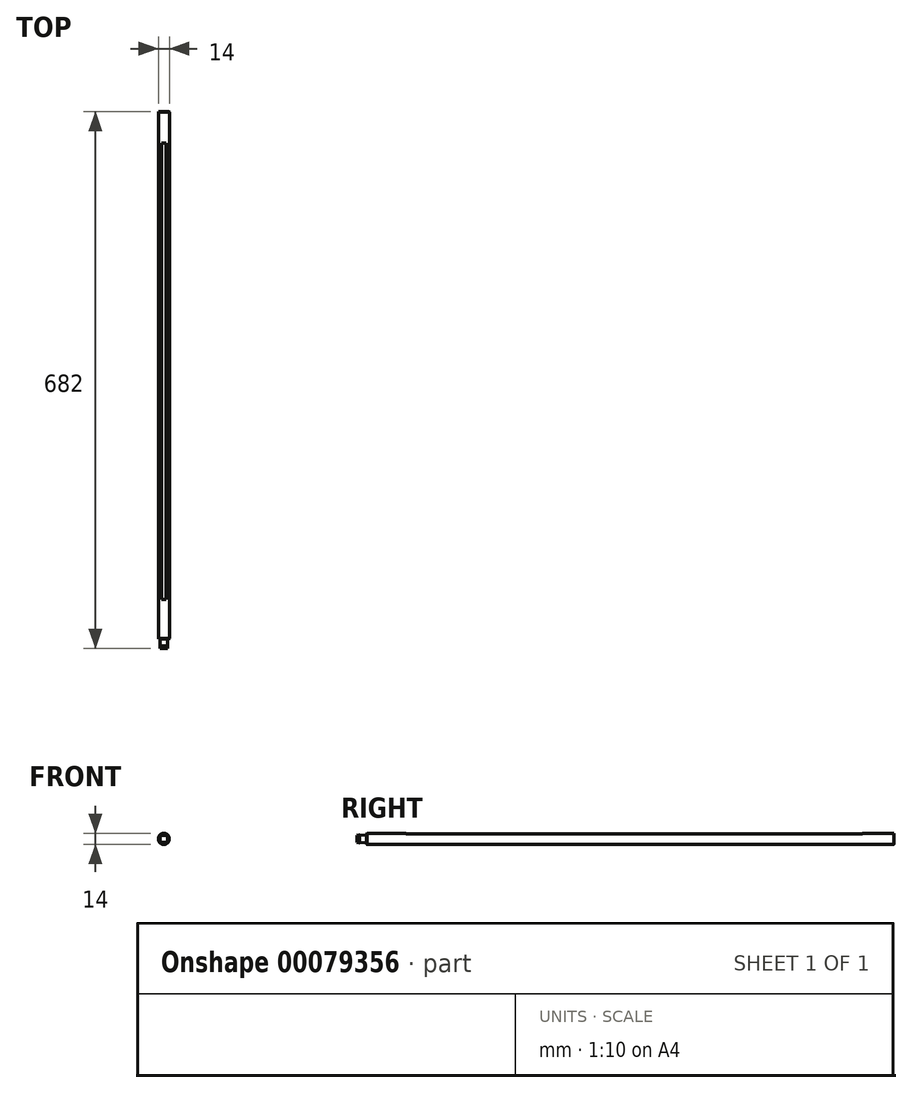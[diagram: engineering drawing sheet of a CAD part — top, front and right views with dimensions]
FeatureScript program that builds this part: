
annotation { "Feature Type Name" : "Feature", "Feature Type Description" : "" }
export const myFeature = defineFeature(function(context is Context, id is Id, definition is map)
    precondition{}
    {
        {
            var Q0;
            Q0=qCreatedBy(makeId("Front.planeOp"),FACE);
            var sketch = newSketch(context, id + "F0", { "sketchPlane" : qUnion([Q0])});
            skCircle(sketch, "E0", {"center": v(0, 0) * mm, "radius": 7 * mm});
            skSolve(sketch);
        }
        {
            var Q0;
            Q0=makeQuery(id+"F0.imprint","IMPRINT",FACE,{"disambiguationData":[TD([[makeQuery(id+"F0.imprint","IMPRINT",EDGE,{"derivedFrom":sQuery(id+"F0.wireOp",EDGE,"E0")}),1.0]])]});
            extrude(context, id + "F1", {"entities" : qUnion([Q0]), "oppositeDirection" : true, "depth" : 670 * mm});
        }
        {
            var Q0;
            Q0=qCreatedBy(makeId("Front.planeOp"),FACE);
            var sketch = newSketch(context, id + "F2", { "sketchPlane" : qUnion([Q0])});
            skLineSegment(sketch, "E1.top", {"start": v(-5, 5) * mm, "end": v(5, 5) * mm});
            skLineSegment(sketch, "E1.left", {"start": v(-5, 4.92) * mm, "end": v(-5, 5) * mm});
            skLineSegment(sketch, "E1.right", {"start": v(5, 4.92) * mm, "end": v(5, 5) * mm});
            skLineSegment(sketch, "E2", {"start": v(-5, 5) * mm, "end": v(-5, -5) * mm});
            skLineSegment(sketch, "E3", {"start": v(-5, -5) * mm, "end": v(5, -5) * mm});
            skLineSegment(sketch, "E4", {"start": v(5, 5) * mm, "end": v(5, -5) * mm});
            skSolve(sketch);
        }
        {
            var Q0;
            {var subQ0=sQuery(id+"F2.wireOp",EDGE,"E1.top");Q0=makeQuery(id+"F2.imprint","IMPRINT",FACE,{"disambiguationData":[TD([[makeQuery(id+"F2.imprint","IMPRINT",EDGE,{"derivedFrom":subQ0}),-1.0]])]});}
            extrude(context, id + "F3", {"entities" : qUnion([Q0]), "depth" : 12 * mm});
        }
        {
            var Q0;
            Q0=makeQuery(id+"F3.opExtrude","SWEPT_FACE",FACE,{"disambiguationData":[OSD([sQuery(id+"F2.wireOp",EDGE,"E4")])]});
            var sketch = newSketch(context, id + "F4", { "sketchPlane" : qUnion([Q0])});
            skLineSegment(sketch, "E5", {"start": v(-12, -4.5) * mm, "end": v(-9, -5) * mm});
            skLineSegment(sketch, "E6", {"start": v(-9, 5) * mm, "end": v(-12, 4.5) * mm});
            skSolve(sketch);
        }
        {
            var Q0;
            {var subQ0=sQuery(id+"F4.wireOp",EDGE,"E5");Q0=makeQuery(id+"F4.imprint","IMPRINT",FACE,{"disambiguationData":[TD([[makeQuery(id+"F4.imprint","IMPRINT",EDGE,{"derivedFrom":subQ0}),-1.0]])]});}
            extrude(context, id + "F5", {"entities" : qUnion([Q0]), "operationType" : NewBodyOperationType.REMOVE, "oppositeDirection" : true, "depth" : 25 * mm});
        }
        {
            var Q0;
            Q0=makeQuery(id+"F3.opExtrude","SWEPT_FACE",FACE,{"disambiguationData":[OSD([sQuery(id+"F2.wireOp",EDGE,"E1.top")])]});
            var sketch = newSketch(context, id + "F6", { "sketchPlane" : qUnion([Q0])});
            skLineSegment(sketch, "E7", {"start": v(4.5, -12) * mm, "end": v(5, -9) * mm});
            skLineSegment(sketch, "E8", {"start": v(-4.5, -12) * mm, "end": v(-5, -9) * mm});
            skSolve(sketch);
        }
        {
            var Q0;
            {var subQ0=sQuery(id+"F6.wireOp",EDGE,"E7");Q0=makeQuery(id+"F6.imprint","IMPRINT",FACE,{"disambiguationData":[TD([[makeQuery(id+"F6.imprint","IMPRINT",EDGE,{"derivedFrom":subQ0}),-1.0]])]});}
            extrude(context, id + "F7", {"entities" : qUnion([Q0]), "operationType" : NewBodyOperationType.REMOVE, "oppositeDirection" : true, "depth" : 25 * mm});
        }
        {
            var Q0;
            {var subQ0=sQuery(id+"F6.wireOp",EDGE,"E8");Q0=makeQuery(id+"F6.imprint","IMPRINT",FACE,{"disambiguationData":[TD([[makeQuery(id+"F6.imprint","IMPRINT",EDGE,{"derivedFrom":subQ0}),1.0]])]});}
            extrude(context, id + "F8", {"entities" : qUnion([Q0]), "operationType" : NewBodyOperationType.REMOVE, "oppositeDirection" : true, "depth" : 25 * mm});
        }
        {
            var Q0;
            {var subQ0=sQuery(id+"F4.wireOp",EDGE,"E6");Q0=makeQuery(id+"F4.imprint","IMPRINT",FACE,{"disambiguationData":[TD([[makeQuery(id+"F4.imprint","IMPRINT",EDGE,{"derivedFrom":subQ0}),-1.0]])]});}
            extrude(context, id + "F9", {"entities" : qUnion([Q0]), "operationType" : NewBodyOperationType.REMOVE, "oppositeDirection" : true, "depth" : 25 * mm});
        }
        {
            var Q0;
            Q0=makeQuery(id+"F3.opExtrude","SWEPT_FACE",FACE,{"disambiguationData":[OSD([sQuery(id+"F2.wireOp",EDGE,"E4")])]});
            var sketch = newSketch(context, id + "F10", { "sketchPlane" : qUnion([Q0])});
            skLineSegment(sketch, "E9", {"start": v(-9, 5) * mm, "end": v(0, 4.5) * mm});
            skLineSegment(sketch, "E10", {"start": v(-9, -5) * mm, "end": v(0, -4.5) * mm});
            skSolve(sketch);
        }
        {
            var Q0;
            Q0=makeQuery(id+"F3.opExtrude","SWEPT_FACE",FACE,{"disambiguationData":[OSD([sQuery(id+"F2.wireOp",EDGE,"E1.top")])]});
            var sketch = newSketch(context, id + "F11", { "sketchPlane" : qUnion([Q0])});
            skLineSegment(sketch, "E11", {"start": v(-5, -9) * mm, "end": v(-4.5, 0) * mm});
            skLineSegment(sketch, "E12", {"start": v(5, -9) * mm, "end": v(4.5, 0) * mm});
            skSolve(sketch);
        }
        {
            var Q0;
            {var subQ0=sQuery(id+"F10.wireOp",EDGE,"E9");Q0=makeQuery(id+"F10.imprint","IMPRINT",FACE,{"disambiguationData":[TD([[makeQuery(id+"F10.imprint","IMPRINT",EDGE,{"derivedFrom":subQ0}),1.0]])]});}
            extrude(context, id + "F12", {"entities" : qUnion([Q0]), "operationType" : NewBodyOperationType.REMOVE, "oppositeDirection" : true, "depth" : 25 * mm});
        }
        {
            var Q0;
            {var subQ0=sQuery(id+"F11.wireOp",EDGE,"E12");Q0=makeQuery(id+"F11.imprint","IMPRINT",FACE,{"disambiguationData":[TD([[makeQuery(id+"F11.imprint","IMPRINT",EDGE,{"derivedFrom":subQ0}),-1.0]])]});}
            extrude(context, id + "F13", {"entities" : qUnion([Q0]), "operationType" : NewBodyOperationType.REMOVE, "oppositeDirection" : true, "depth" : 25 * mm});
        }
        {
            var Q0;
            {var subQ0=sQuery(id+"F10.wireOp",EDGE,"E10");Q0=makeQuery(id+"F10.imprint","IMPRINT",FACE,{"disambiguationData":[TD([[makeQuery(id+"F10.imprint","IMPRINT",EDGE,{"derivedFrom":subQ0}),-1.0]])]});}
            extrude(context, id + "F14", {"entities" : qUnion([Q0]), "operationType" : NewBodyOperationType.REMOVE, "oppositeDirection" : true, "depth" : 25 * mm});
        }
        {
            var Q0;
            {var subQ0=sQuery(id+"F11.wireOp",EDGE,"E11");Q0=makeQuery(id+"F11.imprint","IMPRINT",FACE,{"disambiguationData":[TD([[makeQuery(id+"F11.imprint","IMPRINT",EDGE,{"derivedFrom":subQ0}),1.0]])]});}
            extrude(context, id + "F15", {"entities" : qUnion([Q0]), "operationType" : NewBodyOperationType.REMOVE, "oppositeDirection" : true, "depth" : 25 * mm});
        }
        {
            var Q0;
            Q0=makeQuery(id+"F1.opExtrude","CAP_EDGE",EDGE,{"disambiguationData":[OSD([sQuery(id+"F0.wireOp",EDGE,"E0")])],"isStart":true});
            chamfer(context, id + "F16", {"entities" : qUnion([Q0]), "width" : 0.5 * mm, "tangentPropagation" : true});
        }
        {
            var Q0;
            Q0=qCreatedBy(makeId("Top.planeOp"),FACE);
            cPlane(context, id + "F17", {"entities" : qUnion([Q0]), "cplaneType" : CPlaneType.OFFSET, "offset" : 7 * mm, "width" : 150 * mm, "height" : 150 * mm});
        }
        {
            var Q0;
            Q0=qCreatedBy(id+"F17.planeOp",FACE);
            var sketch = newSketch(context, id + "F18", { "sketchPlane" : qUnion([Q0])});
            skLineSegment(sketch, "E13.bottom", {"start": v(-31.92, 630) * mm, "end": v(36.52, 630) * mm});
            skLineSegment(sketch, "E13.top", {"start": v(-31.92, 50) * mm, "end": v(36.52, 50) * mm});
            skLineSegment(sketch, "E13.left", {"start": v(-31.92, 630) * mm, "end": v(-31.92, 50) * mm});
            skLineSegment(sketch, "E13.right", {"start": v(36.52, 630) * mm, "end": v(36.52, 50) * mm});
            skSolve(sketch);
        }
        {
            var Q0;
            Q0=makeQuery(id+"F18.imprint","IMPRINT",FACE,{"disambiguationData":[TD([[makeQuery(id+"F18.imprint","IMPRINT",EDGE,{"derivedFrom":sQuery(id+"F18.wireOp",EDGE,"E13.bottom")}),-1.0]])]});
            extrude(context, id + "F19", {"entities" : qUnion([Q0]), "operationType" : NewBodyOperationType.REMOVE, "oppositeDirection" : true, "depth" : 0.5 * mm});
        }
        {
            var Q0;
            Q0=makeQuery(id+"F1.opExtrude","CAP_EDGE",EDGE,{"disambiguationData":[OSD([sQuery(id+"F0.wireOp",EDGE,"E0")])],"isStart":false});
            chamfer(context, id + "F20", {"entities" : qUnion([Q0]), "width" : 0.5 * mm, "tangentPropagation" : true});
        }
    });
